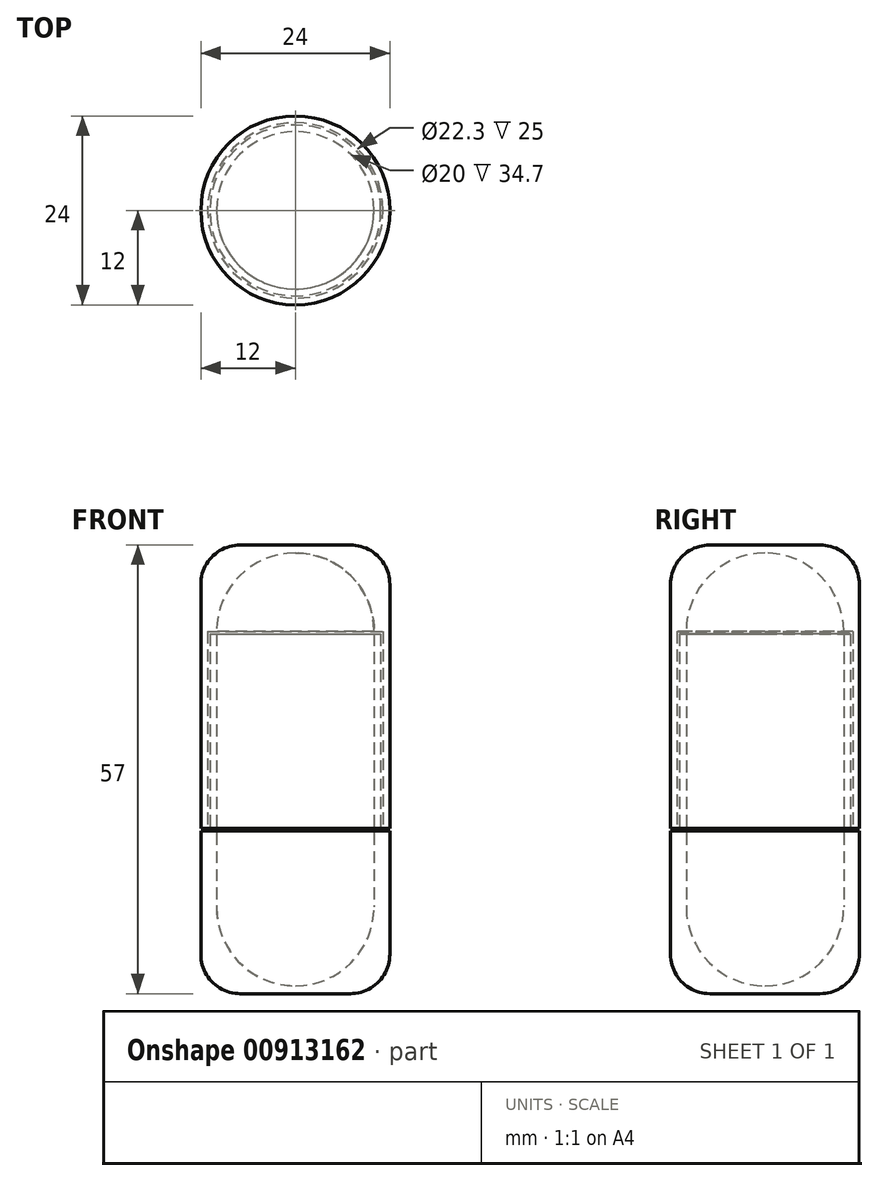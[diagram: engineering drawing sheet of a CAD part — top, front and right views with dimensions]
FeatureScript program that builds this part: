
annotation { "Feature Type Name" : "Feature", "Feature Type Description" : "" }
export const myFeature = defineFeature(function(context is Context, id is Id, definition is map)
    precondition{}
    {
        {
            var Q0;
            Q0=qCreatedBy(makeId("Front.planeOp"),FACE);
            var sketch = newSketch(context, id + "F0", { "sketchPlane" : qUnion([Q0])});
            skArc(sketch, "E0", {"start": v(-10, 0) * mm, "mid": v(-7.07, -7.07) * mm, "end": v(0, -10) * mm});
            skLineSegment(sketch, "E1", {"start": v(-10, 0) * mm, "end": v(-10, 34.7) * mm});
            skPoint(sketch, "E2", {"position": v(0, -10) * mm});
            skLineSegment(sketch, "E3", {"start": v(0, -10) * mm, "end": v(0, 34.7) * mm, "construction": true});
            skLineSegment(sketch, "E4", {"start": v(0, 34.7) * mm, "end": v(-10, 34.7) * mm, "construction": true});
            skLineSegment(sketch, "E5", {"start": v(-10, 34.7) * mm, "end": v(-10.85, 34.7) * mm});
            skLineSegment(sketch, "E6", {"start": v(-10.85, 34.7) * mm, "end": v(-10.85, 9.7) * mm});
            skLineSegment(sketch, "E7", {"start": v(-10.85, -11) * mm, "end": v(0, -11) * mm});
            skLineSegment(sketch, "E8", {"start": v(0, -11) * mm, "end": v(0, -10) * mm});
            skLineSegment(sketch, "E9", {"start": v(-10.85, -11) * mm, "end": v(-12, -11) * mm});
            skLineSegment(sketch, "E10", {"start": v(-12, -11) * mm, "end": v(-12, 9.7) * mm});
            skLineSegment(sketch, "E11", {"start": v(-12, 9.7) * mm, "end": v(-10.85, 9.7) * mm});
            skArc(sketch, "E12", {"start": v(0, 45) * mm, "mid": v(-7.07, 42.07) * mm, "end": v(-10, 35) * mm});
            skPoint(sketch, "E13", {"position": v(0, 45) * mm});
            skLineSegment(sketch, "E14", {"start": v(0, 35) * mm, "end": v(-10, 35) * mm, "construction": true});
            skLineSegment(sketch, "E15", {"start": v(-10, 35) * mm, "end": v(-11.15, 35) * mm});
            skLineSegment(sketch, "E16", {"start": v(-11.15, 35) * mm, "end": v(-11.15, 10) * mm});
            skLineSegment(sketch, "E17", {"start": v(-11.15, 10) * mm, "end": v(-12, 10) * mm});
            skLineSegment(sketch, "E18", {"start": v(-12, 10) * mm, "end": v(-12, 46) * mm});
            skLineSegment(sketch, "E19", {"start": v(-12, 46) * mm, "end": v(0, 46) * mm});
            skLineSegment(sketch, "E20", {"start": v(0, 46) * mm, "end": v(0, 45) * mm});
            skSolve(sketch);
        }
        {
            var Q0;
            Q0=makeQuery(id+"F0.imprint","IMPRINT",FACE,{"disambiguationData":[TD([[makeQuery(id+"F0.imprint","IMPRINT",EDGE,{"derivedFrom":sQuery(id+"F0.wireOp",EDGE,"E0")}),-1.0]])]});
            var Q1;
            Q1=sQuery(id+"F0.wireOp",EDGE,"E3");
            revolve(context, id + "F1", {"surfaceOperationType" : NewSurfaceOperationType.NEW, "entities" : qUnion([Q0]), "axis" : qUnion([Q1]), "revolveType" : RevolveType.FULL});
        }
        {
            var Q0;
            Q0=makeQuery(id+"F0.imprint","IMPRINT",FACE,{"disambiguationData":[TD([[makeQuery(id+"F0.imprint","IMPRINT",EDGE,{"derivedFrom":sQuery(id+"F0.wireOp",EDGE,"E12")}),-1.0]])]});
            var Q1;
            Q1=sQuery(id+"F0.wireOp",EDGE,"E3");
            revolve(context, id + "F2", {"surfaceOperationType" : NewSurfaceOperationType.NEW, "entities" : qUnion([Q0]), "axis" : qUnion([Q1]), "revolveType" : RevolveType.FULL});
        }
        {
            var Q0;
            Q0=makeQuery(id+"F1.opRevolve","SWEPT_FACE",FACE,{"disambiguationData":[OSD([sQuery(id+"F0.wireOp",EDGE,"E7"),sQuery(id+"F0.wireOp",EDGE,"E9")])]});
            var Q1;
            Q1=makeQuery(id+"F2.opRevolve","SWEPT_FACE",FACE,{"disambiguationData":[OSD([sQuery(id+"F0.wireOp",EDGE,"E19")])]});
            fillet(context, id + "F3", {"entities" : qUnion([Q0, Q1]), "radius" : 5 * mm, "tangentPropagation" : true, "allowEdgeOverflow" : false});
        }
    });
